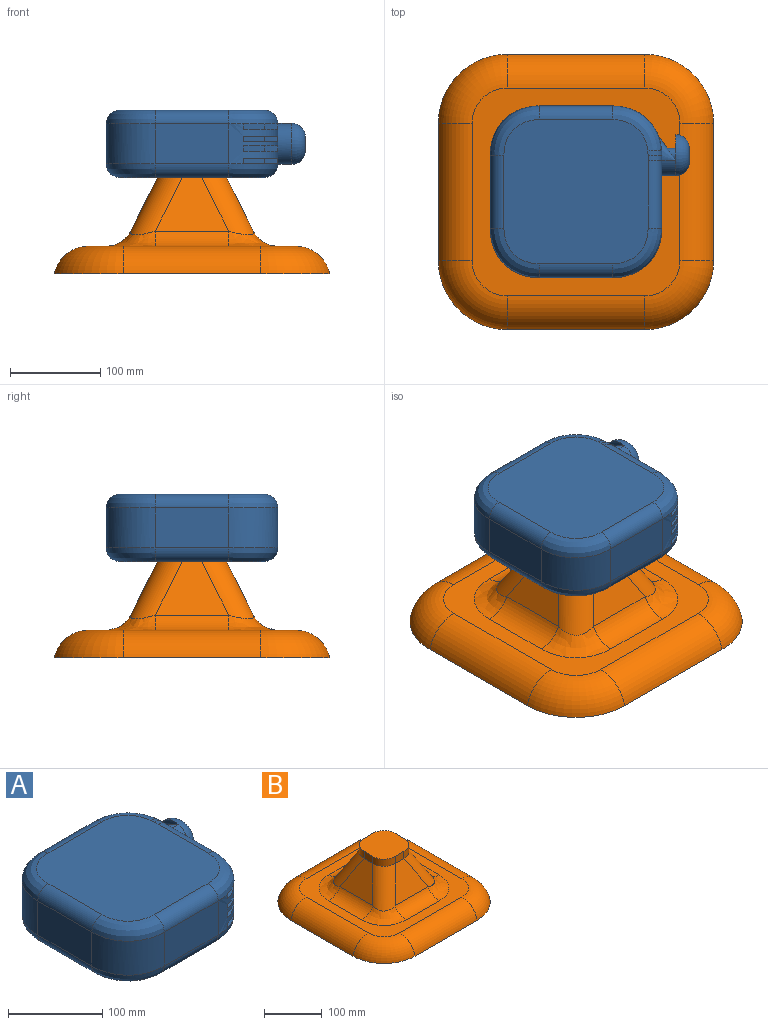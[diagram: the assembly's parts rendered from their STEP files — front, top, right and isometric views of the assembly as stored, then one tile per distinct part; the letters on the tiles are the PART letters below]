
ASSEMBLY  parts=2 mates=1
PART A: 65 faces, bbox 220.6x190.1x74.7 mm
  f0: torus R=7.62mm, axis (1,0,0), area 2605.5mm2, adj f1
  f1: cylinder r=7.62mm len=30.48mm, axis (1,0,0), area 1459.3mm2, adj f0,f2
  f2: plane 15.24x15.24mm, normal (1,0,0), area 182.4mm2, adj f1
  f3: extruded ~54.52x54.52mm, area 2116.4mm2, adj f4,f47,f48,f51,f52,f53,f56,f57
  f4: plane 51.13x6.1mm, normal (1,0,0), area 311.7mm2, adj f3,f5,f7,f47
  f5: plane 22.86x22.86mm, normal (0.71,-0.71,0), area 197.1mm2, adj f4,f6,f7,f47
  f6: plane 15.24x6.1mm, normal (0,-1,0), area 92.9mm2, adj f5,f7,f47,f58
  f7: plane 74.02x38.13mm, normal (0,0,1), area 2054mm2, adj f4,f5,f6,f8,f63
  f8: cylinder r=15.24mm len=75.17mm, axis (0,1,0), area 1799.6mm2, adj f7,f9,f46,f58,f63
  f9: plane 159.62x159.6mm, normal (0,0,-1), area 19048.5mm2, adj f8,f10,f12,f13,f14,f15,f16,f17
  f10: extruded ~27.26x27.26mm, area 658.1mm2, adj f9,f11,f12,f18
  f11: plane 76.2x76.2mm, normal (0,0,-1), area 5206.7mm2, adj f10,f12,f13,f14,f15,f16,f17,f18
  f12: plane 21.68x15.24mm, normal (0,1,0), area 330.3mm2, adj f9,f10,f11,f13
  f13: extruded ~27.26x27.26mm, area 658.1mm2, adj f9,f11,f12,f14
  f14: plane 21.68x15.24mm, normal (1,0,0), area 330.3mm2, adj f9,f11,f13,f15
  f15: extruded ~27.26x27.26mm, area 658.1mm2, adj f9,f11,f14,f16
  f16: plane 21.68x15.24mm, normal (0,-1,0), area 330.3mm2, adj f9,f11,f15,f17
  f17: extruded ~27.26x27.26mm, area 658.1mm2, adj f9,f11,f16,f18
  f18: plane 21.68x15.24mm, normal (-1,0,0), area 330.3mm2, adj f9,f10,f11,f17
  f19: cylinder r=15.24mm len=81.03mm, axis (1,0,0), area 1939.7mm2, adj f9,f45,f62,f63
  f20: bspline ~15.49x15.43mm, area 125.1mm2, adj f9,f21,f46
  f21: bspline ~58.52x53.88mm, area 1731.1mm2, adj f9,f20,f22,f42
  f22: extruded ~54.26x48.67mm, area 2986.7mm2, adj f21,f23,f40,f41
  f23: cylinder r=22.86mm len=44.96mm, axis (-1,0,0), area 696.5mm2, adj f22,f24,f25
  f24: cylinder r=22.86mm len=44.96mm, axis (-1,0,0), area 1004.3mm2, adj f23,f46,f58
  f25: bspline ~15.39x15.36mm, area 137.1mm2, adj f23,f26,f30,f39
  f26: cylinder r=15.24mm len=75.17mm, axis (0,-1,0), area 1799.6mm2, adj f25,f27,f30,f58,f61
  f27: plane 74x38.11mm, normal (0,0,-1), area 2054mm2, adj f26,f28,f29,f60,f61
  f28: plane 15.24x6.1mm, normal (0,-1,0), area 92.9mm2, adj f27,f29,f58,f59
  f29: plane 22.86x22.86mm, normal (0.71,-0.71,0), area 197.1mm2, adj f27,f28,f59,f60
  f30: plane 159.62x159.6mm, normal (0,0,1), area 24255.3mm2, adj f25,f26,f31,f32,f36,f37,f38,f39
  f31: cylinder r=15.24mm len=81.03mm, axis (-1,0,0), area 1939.7mm2, adj f30,f32,f61,f62
  f32: bspline ~62.09x62.09mm, area 1859.2mm2, adj f30,f31,f33,f36
  f33: extruded ~54.52x54.52mm, area 3817mm2, adj f32,f34,f45,f62
  f34: plane 81.03x44.2mm, normal (-1,0,0), area 3581.1mm2, adj f33,f35,f36,f44
  f35: extruded ~54.52x54.52mm, area 3817mm2, adj f34,f37,f40,f43
  f36: cylinder r=15.24mm len=81.03mm, axis (0,1,0), area 1939.7mm2, adj f30,f32,f34,f37
  f37: bspline ~62.09x62.09mm, area 1859.2mm2, adj f30,f35,f36,f38
  f38: cylinder r=15.24mm len=81.03mm, axis (1,0,0), area 1939.7mm2, adj f30,f37,f40,f41
  f39: bspline ~15.5x15.43mm, area 59.9mm2, adj f25,f30,f41
  f40: plane 81.03x44.2mm, normal (0,1,0), area 3581.1mm2, adj f22,f35,f38,f42
  f41: bspline ~58.52x53.88mm, area 1731.1mm2, adj f22,f30,f38,f39
  f42: cylinder r=15.24mm len=81.03mm, axis (-1,0,0), area 1939.7mm2, adj f9,f21,f40,f43
  f43: bspline ~62.09x62.09mm, area 1859.2mm2, adj f9,f35,f42,f44
  f44: cylinder r=15.24mm len=81.03mm, axis (0,-1,0), area 1939.7mm2, adj f9,f34,f43,f45
  f45: bspline ~62.09x62.09mm, area 1859.2mm2, adj f9,f19,f33,f44
  f46: bspline ~15.53x15.46mm, area 137.1mm2, adj f8,f9,f20,f24
  f47: plane 73.99x38.1mm, normal (0,0,-1), area 2054mm2, adj f3,f4,f5,f6,f58
  f48: plane 73.99x38.1mm, normal (0,0,1), area 2054mm2, adj f3,f49,f50,f51,f58
  f49: plane 22.86x22.86mm, normal (0.71,-0.71,0), area 197.1mm2, adj f48,f50,f51,f52
  f50: plane 15.24x6.1mm, normal (0,-1,0), area 92.9mm2, adj f48,f49,f52,f58
  f51: plane 51.13x6.1mm, normal (1,0,0), area 311.7mm2, adj f3,f48,f49,f52
  f52: plane 73.99x38.1mm, normal (0,0,-1), area 2054mm2, adj f3,f49,f50,f51,f58
  f53: plane 73.99x38.1mm, normal (0,0,1), area 2054mm2, adj f3,f54,f55,f56,f58
  f54: plane 22.86x22.86mm, normal (0.71,-0.71,0), area 197.1mm2, adj f53,f55,f56,f57
  f55: plane 15.24x6.1mm, normal (0,-1,0), area 92.9mm2, adj f53,f54,f57,f58
  f56: plane 51.13x6.1mm, normal (1,0,0), area 311.7mm2, adj f3,f53,f54,f57
  f57: plane 73.99x38.1mm, normal (0,0,-1), area 2054mm2, adj f3,f54,f55,f56,f58
  f58: plane 75.17x44.2mm, normal (1,0,0), area 2237.6mm2, adj f3,f6,f8,f24,f26,f28,f47,f48
  f59: plane 73.99x38.1mm, normal (0,0,1), area 2054mm2, adj f3,f28,f29,f58,f60
  f60: plane 51.13x6.1mm, normal (1,0,0), area 311.7mm2, adj f3,f27,f29,f59
  f61: bspline ~62.09x62.09mm, area 1859.2mm2, adj f3,f26,f27,f30,f31
  f62: plane 81.03x44.2mm, normal (0,-1,0), area 3581.1mm2, adj f3,f19,f31,f33
  f63: bspline ~62.09x62.09mm, area 1859.2mm2, adj f3,f7,f8,f9,f19
  f64: cylinder r=22.86mm len=45.72mm, axis (-1,0,0), area 0mm2
PART B: 35 faces, bbox 319x319x129.5 mm
  f0: plane 230.14x230.14mm, normal (0,0,1), area 17937.7mm2, adj f2,f3,f4,f5,f6,f7,f8,f9
  f1: plane 304.8x304.8mm, normal (0,0,-1), area 87918.7mm2, adj f2,f3,f4,f5,f6,f7,f8,f9
  f2: torus R=38.87mm, axis (0,0,-1), area 5009.8mm2, adj f0,f1,f3,f4
  f3: cylinder r=38.1mm len=152.4mm, axis (1,0,0), area 7951.6mm2, adj f0,f1,f2,f5
  f4: cylinder r=38.1mm len=152.4mm, axis (0,1,0), area 7951.6mm2, adj f0,f1,f2,f6
  f5: torus R=38.87mm, axis (0,0,-1), area 5009.8mm2, adj f0,f1,f3,f7
  f6: torus R=38.87mm, axis (0,0,-1), area 5009.8mm2, adj f0,f1,f4,f8
  f7: cylinder r=38.1mm len=152.4mm, axis (0,1,0), area 7951.6mm2, adj f0,f1,f5,f9
  f8: cylinder r=38.1mm len=152.4mm, axis (1,0,0), area 7951.6mm2, adj f0,f1,f6,f9
  f9: torus R=38.87mm, axis (0,0,-1), area 5009.8mm2, adj f0,f1,f7,f8
  f10: plane 81.03x59.35mm, normal (-0.89,0,0.45), area 3407.5mm2, adj f20,f21,f25,f30
  f11: plane 81.03x59.35mm, normal (0,-0.89,0.45), area 3407.5mm2, adj f15,f21,f22,f32
  f12: plane 81.03x59.35mm, normal (0.89,0,0.45), area 3407.5mm2, adj f14,f15,f16,f26
  f13: plane 81.03x59.35mm, normal (0,0.89,0.45), area 3407.5mm2, adj f14,f19,f20,f28
  f14: cylinder r=30.48mm len=71.27mm, axis (-0.41,-0.41,0.82), area 3168.2mm2, adj f12,f13,f17,f27
  f15: cylinder r=30.48mm len=71.27mm, axis (0.41,-0.41,-0.82), area 3168.2mm2, adj f11,f12,f18,f33
  f16: cylinder r=30.48mm len=81.03mm, axis (0,1,0), area 2734.3mm2, adj f0,f12,f17,f18
  f17: bspline ~54.52x54.52mm, area 1977.9mm2, adj f0,f14,f16,f19
  f18: bspline ~54.52x54.52mm, area 1977.9mm2, adj f0,f15,f16,f22
  f19: cylinder r=30.48mm len=81.03mm, axis (-1,0,0), area 2734.3mm2, adj f0,f13,f17,f23
  f20: cylinder r=30.48mm len=71.27mm, axis (-0.41,0.41,-0.82), area 3168.2mm2, adj f10,f13,f23,f29
  f21: cylinder r=30.48mm len=71.27mm, axis (0.41,0.41,0.82), area 3168.2mm2, adj f10,f11,f24,f31
  f22: cylinder r=30.48mm len=81.03mm, axis (-1,0,0), area 2734.3mm2, adj f0,f11,f18,f24
  f23: bspline ~54.52x54.52mm, area 1977.9mm2, adj f0,f19,f20,f25
  f24: bspline ~54.52x54.52mm, area 1977.9mm2, adj f0,f21,f22,f25
  f25: cylinder r=30.48mm len=81.03mm, axis (0,1,0), area 2734.3mm2, adj f0,f10,f23,f24
  f26: plane 21.68x15.24mm, normal (1,0,0), area 330.3mm2, adj f12,f27,f33,f34
  f27: extruded ~27.26x27.26mm, area 658.1mm2, adj f14,f26,f28,f34
  f28: plane 21.68x15.24mm, normal (0,1,0), area 330.3mm2, adj f13,f27,f29,f34
  f29: extruded ~27.26x27.26mm, area 658.1mm2, adj f20,f28,f30,f34
  f30: plane 21.68x15.24mm, normal (-1,0,0), area 330.3mm2, adj f10,f29,f31,f34
  f31: extruded ~27.26x27.26mm, area 658.1mm2, adj f21,f30,f32,f34
  f32: plane 21.68x15.24mm, normal (0,-1,0), area 330.3mm2, adj f11,f31,f33,f34
  f33: extruded ~27.26x27.26mm, area 658.1mm2, adj f15,f26,f32,f34
  f34: plane 76.2x76.2mm, normal (0,0,1), area 5206.7mm2, adj f26,f27,f28,f29,f30,f31,f32,f33
PLACE A t=(-87.03,-14.62,59.38)mm
PLACE B t=(-87.03,-14.62,59.38)mm fixed
MATE fastened A.f11 <-> B.f34  axis (0,0,-1) through (65.37,137.78,181.3)mm
